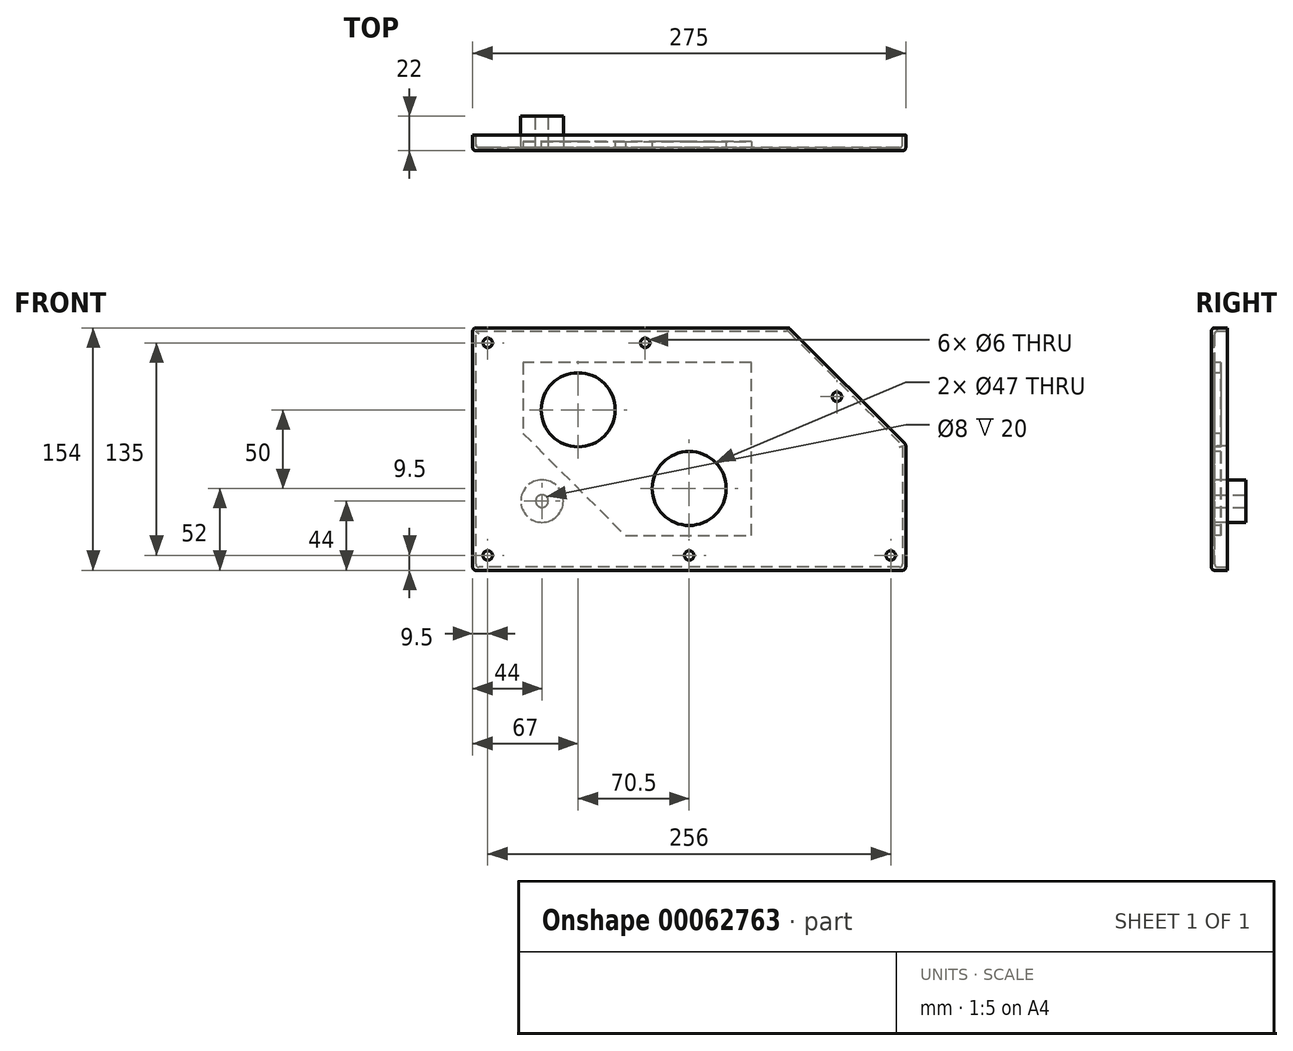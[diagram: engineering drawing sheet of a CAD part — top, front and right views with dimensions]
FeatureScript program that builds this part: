
annotation { "Feature Type Name" : "Feature", "Feature Type Description" : "" }
export const myFeature = defineFeature(function(context is Context, id is Id, definition is map)
    precondition{}
    {
        {
            var Q0;
            Q0=qCreatedBy(makeId("Front.planeOp"),FACE);
            var sketch = newSketch(context, id + "F0", { "sketchPlane" : qUnion([Q0])});
            skLineSegment(sketch, "E0", {"start": v(0, 0) * mm, "end": v(0, 154) * mm});
            skLineSegment(sketch, "E1", {"start": v(0, 154) * mm, "end": v(201, 154) * mm});
            skLineSegment(sketch, "E2", {"start": v(201, 154) * mm, "end": v(275, 80) * mm});
            skLineSegment(sketch, "E3", {"start": v(275, 80) * mm, "end": v(275, 0) * mm});
            skLineSegment(sketch, "E4", {"start": v(275, 0) * mm, "end": v(0, 0) * mm});
            skSolve(sketch);
        }
        {
            var Q0;
            Q0=makeQuery(id+"F0.imprint","IMPRINT",FACE,{"disambiguationData":[TD([[makeQuery(id+"F0.imprint","IMPRINT",EDGE,{"derivedFrom":sQuery(id+"F0.wireOp",EDGE,"E0")}),-1.0]])]});
            extrude(context, id + "F1", {"entities" : qUnion([Q0]), "depth" : 10 * mm});
        }
        {
            var Q0;
            Q0=makeQuery(id+"F1.opExtrude","CAP_FACE",FACE,{"disambiguationData":[OSD([sQuery(id+"F0.wireOp",EDGE,"E0"),sQuery(id+"F0.wireOp",EDGE,"E1"),sQuery(id+"F0.wireOp",EDGE,"E2"),sQuery(id+"F0.wireOp",EDGE,"E3"),sQuery(id+"F0.wireOp",EDGE,"E4")])],"isStart":true});
            shell(context, id + "F2", {"entities" : qUnion([Q0]), "thickness" : 2 * mm});
        }
        {
            var Q0;
            Q0=makeQuery(id+"F2.opShell","OFFSET_FACE",FACE,{"disambiguationData":[OSD([sQuery(id+"F0.wireOp",EDGE,"E0"),sQuery(id+"F0.wireOp",EDGE,"E1"),sQuery(id+"F0.wireOp",EDGE,"E2"),sQuery(id+"F0.wireOp",EDGE,"E3"),sQuery(id+"F0.wireOp",EDGE,"E4")])]});
            var sketch = newSketch(context, id + "F3", { "sketchPlane" : qUnion([Q0])});
            skCircle(sketch, "E5", {"center": v(-67, 102) * mm, "radius": 23.5 * mm});
            skCircle(sketch, "E6", {"center": v(-137.5, 52) * mm, "radius": 23.5 * mm});
            skSolve(sketch);
        }
        {
            var Q0;
            Q0=makeQuery(id+"F2.opShell","OFFSET_FACE",FACE,{"disambiguationData":[OSD([sQuery(id+"F0.wireOp",EDGE,"E0"),sQuery(id+"F0.wireOp",EDGE,"E1"),sQuery(id+"F0.wireOp",EDGE,"E2"),sQuery(id+"F0.wireOp",EDGE,"E3"),sQuery(id+"F0.wireOp",EDGE,"E4")])]});
            var sketch = newSketch(context, id + "F4", { "sketchPlane" : qUnion([Q0])});
            skLineSegment(sketch, "E7", {"start": v(-32, 132) * mm, "end": v(-32, 87) * mm});
            skLineSegment(sketch, "E8", {"start": v(-32, 87) * mm, "end": v(-97, 22) * mm});
            skLineSegment(sketch, "E9", {"start": v(-97, 22) * mm, "end": v(-177, 22) * mm});
            skLineSegment(sketch, "E10", {"start": v(-177, 22) * mm, "end": v(-177, 132) * mm});
            skLineSegment(sketch, "E11", {"start": v(-177, 132) * mm, "end": v(-32, 132) * mm});
            skSolve(sketch);
        }
        {
            var Q0;
            Q0=qSketchRegion(id+"F4",true);
            var Q1;
            Q1=makeQuery(id+"F4.imprint","IMPRINT",FACE,{"disambiguationData":[TD([[makeQuery(id+"F4.imprint","IMPRINT",EDGE,{"derivedFrom":sQuery(id+"F4.wireOp",EDGE,"E7")}),-1.0]])]});
            extrude(context, id + "F5", {"entities" : qUnion([Q0, Q1]), "operationType" : NewBodyOperationType.ADD, "depth" : 4 * mm});
        }
        {
            var Q0;
            Q0=qSketchRegion(id+"F3",true);
            extrude(context, id + "F6", {"entities" : qUnion([Q0]), "operationType" : NewBodyOperationType.REMOVE, "endBound" : BoundingType.THROUGH_ALL, "depth" : 25 * mm, "hasSecondDirection" : true, "secondDirectionBound" : SecondDirectionBoundingType.THROUGH_ALL, "secondDirectionOppositeDirection" : true, "secondDirectionDepth" : 25 * mm});
        }
        {
            var Q0;
            Q0=makeQuery(id+"F2.opShell","OFFSET_FACE",FACE,{"disambiguationData":[OSD([sQuery(id+"F0.wireOp",EDGE,"E0"),sQuery(id+"F0.wireOp",EDGE,"E1"),sQuery(id+"F0.wireOp",EDGE,"E2"),sQuery(id+"F0.wireOp",EDGE,"E3"),sQuery(id+"F0.wireOp",EDGE,"E4")])]});
            var sketch = newSketch(context, id + "F7", { "sketchPlane" : qUnion([Q0])});
            skCircle(sketch, "E12", {"center": v(-44, 44) * mm, "radius": 13.5 * mm});
            skSolve(sketch);
        }
        {
            var Q0;
            Q0=qSketchRegion(id+"F7",true);
            extrude(context, id + "F8", {"entities" : qUnion([Q0]), "operationType" : NewBodyOperationType.ADD, "depth" : 20 * mm});
        }
        {
            var Q0;
            Q0=makeQuery(id+"F8.opExtrude","CAP_FACE",FACE,{"disambiguationData":[OSD([sQuery(id+"F7.wireOp",EDGE,"E12")])],"isStart":false});
            var sketch = newSketch(context, id + "F9", { "sketchPlane" : qUnion([Q0])});
            skPoint(sketch, "E13", {"position": v(-44, 44) * mm});
            skCircle(sketch, "E14", {"center": v(-44, 44) * mm, "radius": 4 * mm});
            skSolve(sketch);
        }
        {
            var Q0;
            Q0=makeQuery(id+"F9.imprint","IMPRINT",FACE,{"disambiguationData":[TD([[makeQuery(id+"F9.imprint","IMPRINT",EDGE,{"derivedFrom":sQuery(id+"F9.wireOp",EDGE,"E14")}),1.0]])]});
            var Q1;
            Q1=makeQuery(id+"F2.opShell","OFFSET_FACE",FACE,{"disambiguationData":[OSD([sQuery(id+"F0.wireOp",EDGE,"E0"),sQuery(id+"F0.wireOp",EDGE,"E1"),sQuery(id+"F0.wireOp",EDGE,"E2"),sQuery(id+"F0.wireOp",EDGE,"E3"),sQuery(id+"F0.wireOp",EDGE,"E4")])]});
            extrude(context, id + "F10", {"entities" : qUnion([Q0]), "operationType" : NewBodyOperationType.REMOVE, "endBound" : BoundingType.UP_TO_SURFACE, "oppositeDirection" : true, "endBoundEntityFace" : qUnion([Q1]), "depth" : 25 * mm});
        }
        {
            var Q0;
            Q0=makeQuery(id+"F1.opExtrude","CAP_FACE",FACE,{"disambiguationData":[OSD([sQuery(id+"F0.wireOp",EDGE,"E0"),sQuery(id+"F0.wireOp",EDGE,"E1"),sQuery(id+"F0.wireOp",EDGE,"E2"),sQuery(id+"F0.wireOp",EDGE,"E3"),sQuery(id+"F0.wireOp",EDGE,"E4")])],"isStart":false});
            var sketch = newSketch(context, id + "F11", { "sketchPlane" : qUnion([Q0])});
            skLineSegment(sketch, "E15.0", {"start": v(9.5, 9.5) * mm, "end": v(265.5, 9.5) * mm, "construction": true});
            skLineSegment(sketch, "E15.1", {"start": v(9.5, 144.5) * mm, "end": v(9.5, 9.5) * mm, "construction": true});
            skLineSegment(sketch, "E15.2", {"start": v(265.5, 9.5) * mm, "end": v(265.5, 76.06) * mm, "construction": true});
            skLineSegment(sketch, "E15.3", {"start": v(265.5, 76.06) * mm, "end": v(197.06, 144.5) * mm, "construction": true});
            skLineSegment(sketch, "E15.4", {"start": v(197.06, 144.5) * mm, "end": v(9.5, 144.5) * mm, "construction": true});
            skPoint(sketch, "E16", {"position": v(9.5, 144.5) * mm});
            skPoint(sketch, "E17", {"position": v(109.5, 144.5) * mm});
            skPoint(sketch, "E18", {"position": v(231.28, 110.28) * mm});
            skPoint(sketch, "E19", {"position": v(265.5, 9.5) * mm});
            skPoint(sketch, "E20", {"position": v(137.5, 9.5) * mm});
            skPoint(sketch, "E21", {"position": v(9.5, 9.5) * mm});
            skSolve(sketch);
        }
        {
            var Q0;
            Q0=sQuery(id+"F11.wireOp",VERTEX,"E16");
            var Q1;
            Q1=sQuery(id+"F11.wireOp",VERTEX,"E17");
            var Q2;
            Q2=sQuery(id+"F11.wireOp",VERTEX,"E18");
            var Q3;
            Q3=sQuery(id+"F11.wireOp",VERTEX,"E19");
            var Q4;
            Q4=sQuery(id+"F11.wireOp",VERTEX,"E20");
            var Q5;
            Q5=sQuery(id+"F11.wireOp",VERTEX,"E21");
            var Q6;
            Q6=makeQuery(id+"F1.opExtrude","SWEPT_BODY",BODY,{"disambiguationData":[OSD([sQuery(id+"F0.wireOp",EDGE,"E0"),sQuery(id+"F0.wireOp",EDGE,"E1"),sQuery(id+"F0.wireOp",EDGE,"E2"),sQuery(id+"F0.wireOp",EDGE,"E3"),sQuery(id+"F0.wireOp",EDGE,"E4")])]});
            hole(context, id + "F12", {"style" : HoleStyle.SIMPLE, "holeDiameter" : 6 * mm, "endStyle" : HoleEndStyle.THROUGH, "locations" : qUnion([Q0, Q1, Q2, Q3, Q4, Q5]), "scope" : qUnion([Q6])});
        }
        {
            var Q0;
            Q0=makeQuery(id+"F1.opExtrude","CAP_EDGE",EDGE,{"disambiguationData":[OSD([sQuery(id+"F0.wireOp",EDGE,"E0")])],"isStart":false});
            var Q1;
            Q1=makeQuery(id+"F1.opExtrude","CAP_EDGE",EDGE,{"disambiguationData":[OSD([sQuery(id+"F0.wireOp",EDGE,"E4")])],"isStart":false});
            var Q2;
            Q2=makeQuery(id+"F1.opExtrude","CAP_EDGE",EDGE,{"disambiguationData":[OSD([sQuery(id+"F0.wireOp",EDGE,"E2")])],"isStart":false});
            var Q3;
            Q3=makeQuery(id+"F1.opExtrude","CAP_EDGE",EDGE,{"disambiguationData":[OSD([sQuery(id+"F0.wireOp",EDGE,"E3")])],"isStart":false});
            var Q4;
            Q4=makeQuery(id+"F1.opExtrude","SWEPT_EDGE",EDGE,{"disambiguationData":[OSD([sQuery(id+"F0.wireOp",EDGE,"E3"),sQuery(id+"F0.wireOp",EDGE,"E4")])]});
            var Q5;
            Q5=makeQuery(id+"F1.opExtrude","SWEPT_EDGE",EDGE,{"disambiguationData":[OSD([sQuery(id+"F0.wireOp",EDGE,"E2"),sQuery(id+"F0.wireOp",EDGE,"E3")])]});
            var Q6;
            Q6=makeQuery(id+"F1.opExtrude","SWEPT_EDGE",EDGE,{"disambiguationData":[OSD([sQuery(id+"F0.wireOp",EDGE,"E1"),sQuery(id+"F0.wireOp",EDGE,"E2")])]});
            var Q7;
            Q7=makeQuery(id+"F1.opExtrude","SWEPT_EDGE",EDGE,{"disambiguationData":[OSD([sQuery(id+"F0.wireOp",EDGE,"E0"),sQuery(id+"F0.wireOp",EDGE,"E4")])]});
            var Q8;
            Q8=makeQuery(id+"F1.opExtrude","CAP_EDGE",EDGE,{"disambiguationData":[OSD([sQuery(id+"F0.wireOp",EDGE,"E1")])],"isStart":false});
            var Q9;
            Q9=makeQuery(id+"F1.opExtrude","SWEPT_EDGE",EDGE,{"disambiguationData":[OSD([sQuery(id+"F0.wireOp",EDGE,"E0"),sQuery(id+"F0.wireOp",EDGE,"E1")])]});
            fillet(context, id + "F13", {"entities" : qUnion([Q0, Q1, Q2, Q3, Q4, Q5, Q6, Q7, Q8, Q9]), "radius" : 2 * mm, "tangentPropagation" : true, "allowEdgeOverflow" : false});
        }
        {
            var Q0;
            Q0=makeQuery(id+"F2.opShell","OFFSET_EDGE",EDGE,{"disambiguationData":[OSD([sQuery(id+"F0.wireOp",EDGE,"E3"),sQuery(id+"F0.wireOp",EDGE,"E4")])]});
            var Q1;
            {var subQ0=sQuery(id+"F0.wireOp",EDGE,"E4");Q1=makeQuery(id+"F2.opShell","OFFSET_EDGE",EDGE,{"disambiguationData":[OSD([subQ0]),TDD([makeQuery(id+"F1.opExtrude","CAP_EDGE",EDGE,{"disambiguationData":[OSD([subQ0])],"isStart":false})])]});}
            var Q2;
            {var subQ0=sQuery(id+"F0.wireOp",EDGE,"E3");Q2=makeQuery(id+"F2.opShell","OFFSET_EDGE",EDGE,{"disambiguationData":[OSD([subQ0]),TDD([makeQuery(id+"F1.opExtrude","CAP_EDGE",EDGE,{"disambiguationData":[OSD([subQ0])],"isStart":false})])]});}
            var Q3;
            {var subQ0=sQuery(id+"F0.wireOp",EDGE,"E2");Q3=makeQuery(id+"F2.opShell","OFFSET_EDGE",EDGE,{"disambiguationData":[OSD([subQ0]),TDD([makeQuery(id+"F1.opExtrude","CAP_EDGE",EDGE,{"disambiguationData":[OSD([subQ0])],"isStart":false})])]});}
            var Q4;
            Q4=makeQuery(id+"F2.opShell","OFFSET_EDGE",EDGE,{"disambiguationData":[OSD([sQuery(id+"F0.wireOp",EDGE,"E1"),sQuery(id+"F0.wireOp",EDGE,"E2")])]});
            var Q5;
            {var subQ0=sQuery(id+"F0.wireOp",EDGE,"E1");Q5=makeQuery(id+"F2.opShell","OFFSET_EDGE",EDGE,{"disambiguationData":[OSD([subQ0]),TDD([makeQuery(id+"F1.opExtrude","CAP_EDGE",EDGE,{"disambiguationData":[OSD([subQ0])],"isStart":false})])]});}
            var Q6;
            Q6=makeQuery(id+"F2.opShell","OFFSET_EDGE",EDGE,{"disambiguationData":[OSD([sQuery(id+"F0.wireOp",EDGE,"E0"),sQuery(id+"F0.wireOp",EDGE,"E4")])]});
            var Q7;
            {var subQ0=sQuery(id+"F0.wireOp",EDGE,"E0");Q7=makeQuery(id+"F2.opShell","OFFSET_EDGE",EDGE,{"disambiguationData":[OSD([subQ0]),TDD([makeQuery(id+"F1.opExtrude","CAP_EDGE",EDGE,{"disambiguationData":[OSD([subQ0])],"isStart":false})])]});}
            fillet(context, id + "F14", {"entities" : qUnion([Q0, Q1, Q2, Q3, Q4, Q5, Q6, Q7]), "radius" : 2 * mm, "tangentPropagation" : true, "allowEdgeOverflow" : false});
        }
    });
